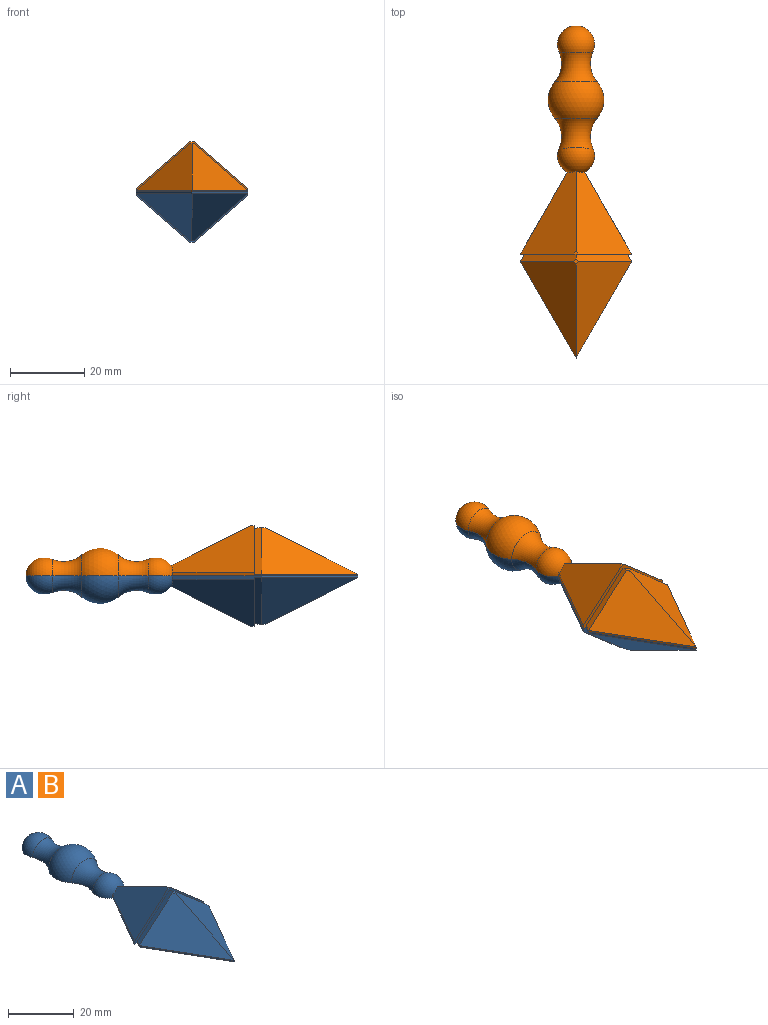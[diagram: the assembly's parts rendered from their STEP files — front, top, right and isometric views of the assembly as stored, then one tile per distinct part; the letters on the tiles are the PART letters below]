
ASSEMBLY  parts=2 mates=1
PART A: 23 faces, bbox 30x89.4x13.5 mm
  f0: plane 89.41x30mm, normal (0,0,-1), area 1189mm2, adj f1,f2,f3,f4,f5,f11,f12,f13
  f1: sphere r=5mm, area 110.4mm2, adj f0,f19,f22
  f2: plane 2x1.15mm, normal (0.87,0.5,0), area 1.2mm2, adj f0,f5,f10,f11
  f3: plane 2x1.15mm, normal (-0.87,0.5,0), area 1.2mm2, adj f0,f4,f9,f11
  f4: plane 25.98x15mm, normal (-0.87,-0.5,0), area 15mm2, adj f0,f3,f5,f7
  f5: plane 25.98x15mm, normal (0.87,-0.5,0), area 15mm2, adj f0,f2,f4,f8
  f6: plane 1.96x1.13mm, normal (0,0,1), area 1.1mm2, adj f7,f8,f9,f10
  f7: plane 25.98x15mm, normal (-0.61,-0.35,0.71), area 275.2mm2, adj f4,f6,f8,f9
  f8: plane 25.98x15mm, normal (0.61,-0.35,0.71), area 275.2mm2, adj f5,f6,f7,f10
  f9: plane 15x12.5mm, normal (-0.61,0.35,0.71), area 40.4mm2, adj f3,f6,f7,f10,f11
  f10: plane 15x12.5mm, normal (0.61,0.35,0.71), area 40.4mm2, adj f2,f6,f8,f9,f11
  f11: plane 30x13.5mm, normal (0,-1,0), area 44.7mm2, adj f0,f2,f3,f9,f10,f12,f13,f14
  f12: plane 22.12x12.77mm, normal (0.87,0.5,0), area 25.5mm2, adj f0,f11,f16,f20
  f13: plane 22.12x12.77mm, normal (-0.87,0.5,0), area 25.5mm2, adj f0,f11,f15,f20
  f14: plane 1.13x0.98mm, normal (0,0,1), area 0.6mm2, adj f11,f15,f16
  f15: plane 22.35x15mm, normal (-0.61,0.35,0.71), area 269mm2, adj f11,f13,f14,f16,f20
  f16: plane 22.35x15mm, normal (0.61,0.35,0.71), area 269mm2, adj f11,f12,f14,f15,f20
  f17: torus R=11.36mm, axis (0,1,0), area 116.5mm2, adj f0,f18,f20
  f18: sphere r=7.5mm, area 230.7mm2, adj f0,f17,f19
  f19: torus R=11.36mm, axis (0,1,0), area 116.5mm2, adj f0,f1,f18
  f20: sphere r=5mm, area 101.8mm2, adj f0,f12,f13,f15,f16,f17
  f21: plane 1.5x0.75mm, normal (0,1,0), area 0.9mm2, adj f0,f22
  f22: cylinder r=0.75mm len=19.94mm, axis (0,1,0), area 47mm2, adj f0,f1,f21
PART B: same geometry as A
PLACE A rot(axis=(0,1,0),180deg) t=(-1.22,35.35,-17.83)mm
PLACE B t=(-1.22,35.35,-17.83)mm
MATE parallel A.f0 <-> B.f0  axis (0,0,1) through (-1.22,5.36,-17.83)mm
